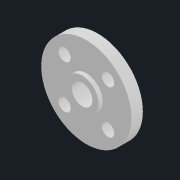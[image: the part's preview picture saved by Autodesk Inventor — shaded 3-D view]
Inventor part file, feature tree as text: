
AUTODESK INVENTOR PART (.ipt)
format: ipt  version: 2022.2 (Build 262287010, 287A)  size: 108,032 bytes
history: native  units: mm
features: sketch x3, extrude x2, hole x1
ambient origin geometry x8: Origin, YZ Plane, XZ Plane, XY Plane, X Axis, Y Axis, Z Axis, Center Point
bodies: Solid1 (feature_tree)
feature tree (6):
  extrude  "Extrusion1"  Depth=5.0mm
  hole  "Hole1"  [1 undecoded]
  extrude  "Extrusion2"  Depth=1.0mm
  sketch  "Sketch1"  dims[d0=22.0mm d1=5.0mm]
  sketch  "Sketch2"  dims[d2=2.8mm d3=0.0mm d4=15.0mm]
  sketch  "Sketch3"  dims[d5=90.0deg d6=3.0mm d7=6.0mm d8=4.0mm d9=2.0mm d10=90.0deg d11=8.0mm d12=20.594885mm d13=8.0mm d14=1.0mm d15=0.0mm]
note: 1 required parameter value undecoded (feature->parameter linkage not recoverable at this tier; creation-order binding heuristic only, values carry confidence <= 0.55)
